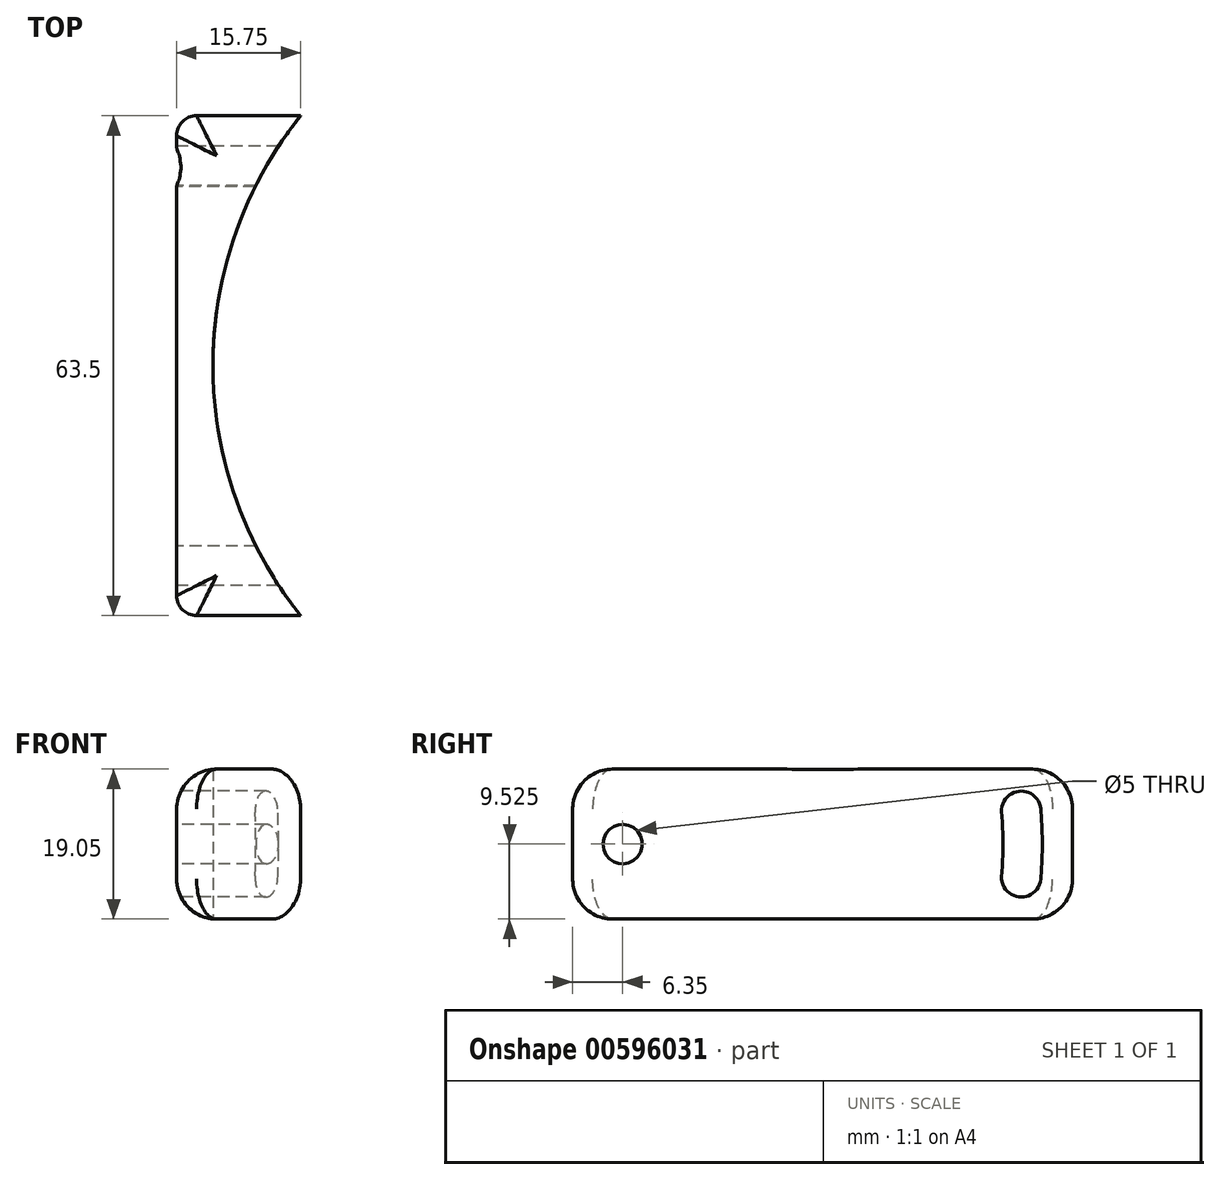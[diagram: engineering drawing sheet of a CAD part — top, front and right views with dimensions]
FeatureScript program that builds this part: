
annotation { "Feature Type Name" : "Feature", "Feature Type Description" : "" }
export const myFeature = defineFeature(function(context is Context, id is Id, definition is map)
    precondition{}
    {
        {
            var Q0;
            Q0=qCreatedBy(makeId("Top.planeOp"),FACE);
            var sketch = newSketch(context, id + "F0", { "sketchPlane" : qUnion([Q0])});
            skArc(sketch, "E0", {"start": v(-39.66, 31.75) * mm, "mid": v(-50.8, 0) * mm, "end": v(-39.66, -31.75) * mm});
            skLineSegment(sketch, "E1", {"start": v(-55.4, 29.21) * mm, "end": v(-55.4, -29.21) * mm});
            skPoint(sketch, "E2", {"position": v(-55.4, 0) * mm});
            skLineSegment(sketch, "E3", {"start": v(-52.87, 31.75) * mm, "end": v(-39.66, 31.75) * mm});
            skLineSegment(sketch, "E4", {"start": v(-52.87, -31.75) * mm, "end": v(-39.66, -31.75) * mm});
            skPoint(sketch, "E5.visualSharp", {"position": v(-55.4, 31.75) * mm});
            skArc(sketch, "E5.filletArc", {"start": v(-52.87, 31.75) * mm, "mid": v(-54.67, 31) * mm, "end": v(-55.4, 29.21) * mm});
            skPoint(sketch, "E6.visualSharp", {"position": v(-55.4, -31.75) * mm});
            skArc(sketch, "E6.filletArc", {"start": v(-55.4, -29.21) * mm, "mid": v(-54.67, -31) * mm, "end": v(-52.87, -31.75) * mm});
            skSolve(sketch);
        }
        {
            var Q0;
            Q0=makeQuery(id+"F0.imprint","IMPRINT",FACE,{"disambiguationData":[TD([[makeQuery(id+"F0.imprint","IMPRINT",EDGE,{"derivedFrom":sQuery(id+"F0.wireOp",EDGE,"E0")}),-1.0]])]});
            extrude(context, id + "F1", {"entities" : qUnion([Q0]), "depth" : 19.05 * mm, "offsetDistance" : 25.4 * mm});
        }
        {
            var Q0;
            Q0=makeQuery(id+"F1.opExtrude","SWEPT_FACE",FACE,{"disambiguationData":[OSD([sQuery(id+"F0.wireOp",EDGE,"E1")])]});
            cPlane(context, id + "F2", {"entities" : qUnion([Q0]), "cplaneType" : CPlaneType.OFFSET, "offset" : 0 * mm, "width" : 152.4 * mm, "height" : 152.4 * mm});
        }
        {
            var Q0;
            Q0=qCreatedBy(id+"F2.planeOp",FACE);
            var sketch = newSketch(context, id + "F3", { "sketchPlane" : qUnion([Q0])});
            skLineSegment(sketch, "E7", {"start": v(-31.75, 19.05) * mm, "end": v(-31.75, 0) * mm});
            skPoint(sketch, "E8", {"position": v(-31.75, 9.53) * mm});
            skLineSegment(sketch, "E9", {"start": v(-31.75, 9.53) * mm, "end": v(26.81, 9.53) * mm});
            skPoint(sketch, "E10", {"position": v(-25.4, 9.53) * mm});
            skPoint(sketch, "E11", {"position": v(25.4, 9.53) * mm});
            skArc(sketch, "E12", {"start": v(-22.73, 13.55) * mm, "mid": v(-25.02, 16.25) * mm, "end": v(-27.72, 13.97) * mm});
            skArc(sketch, "E13.MirrorCS", {"start": v(-22.73, 5.5) * mm, "mid": v(-25.02, 2.8) * mm, "end": v(-27.72, 5.08) * mm});
            skPoint(sketch, "E14.MirrorCS.end.orphan", {"position": v(-27.9, 9.53) * mm});
            skPoint(sketch, "E14.MirrorCS.start.orphan", {"position": v(-27.72, 5.08) * mm});
            skPoint(sketch, "E15.MirrorCS.end.orphan", {"position": v(-22.9, 9.53) * mm});
            skPoint(sketch, "E15.MirrorCS.start.orphan", {"position": v(-22.73, 5.5) * mm});
            skArc(sketch, "E16", {"start": v(-22.73, 13.55) * mm, "mid": v(-22.9, 9.53) * mm, "end": v(-22.73, 5.5) * mm});
            skArc(sketch, "E17", {"start": v(-27.72, 13.97) * mm, "mid": v(-27.9, 9.53) * mm, "end": v(-27.72, 5.08) * mm});
            skSolve(sketch);
        }
        {
            var Q0;
            Q0=sQuery(id+"F3.wireOp",VERTEX,"E11");
            var Q1;
            Q1=makeQuery(id+"F1.opExtrude","SWEPT_BODY",BODY,{"disambiguationData":[OSD([sQuery(id+"F0.wireOp",EDGE,"E0"),sQuery(id+"F0.wireOp",EDGE,"E1"),sQuery(id+"F0.wireOp",EDGE,"E3"),sQuery(id+"F0.wireOp",EDGE,"E4")])]});
            hole(context, id + "F4", {"style" : HoleStyle.SIMPLE, "endStyle" : HoleEndStyle.BLIND, "standardTappedOrClearance" : lookupTablePath({ "standard" : "ISO", "engagement" : "75%", "pitch" : "1 mm", "size" : "M6", "type" : "Tapped" }), "standardBlindInLast" : lookupTablePath({ "standard" : "ISO", "engagement" : "75%", "pitch" : "1 mm", "size" : "M6", "type" : "Tapped" }), "holeDiameter" : 5 * mm, "showTappedDepth" : true, "holeDepth" : 15.7 * mm, "isTappedThrough" : true, "tappedDepth" : 12.7 * mm, "tapClearance" : 3, "locations" : qUnion([Q0]), "scope" : qUnion([Q1]), "majorDiameter" : 6 * mm});
        }
        {
            var Q0;
            Q0=qSketchRegion(id+"F3",true);
            extrude(context, id + "F5", {"entities" : qUnion([Q0]), "operationType" : NewBodyOperationType.REMOVE, "oppositeDirection" : true, "depth" : 25.4 * mm, "offsetDistance" : 25.4 * mm});
        }
        {
            var Q0;
            Q0=makeQuery(id+"F1.opExtrude","CAP_EDGE",EDGE,{"disambiguationData":[OSD([sQuery(id+"F0.wireOp",EDGE,"E1")])],"isStart":false});
            var Q1;
            Q1=makeQuery(id+"F1.opExtrude","CAP_EDGE",EDGE,{"disambiguationData":[OSD([sQuery(id+"F0.wireOp",EDGE,"E1")])],"isStart":true});
            fillet(context, id + "F6", {"entities" : qUnion([Q0, Q1]), "radius" : 5.08 * mm, "tangentPropagation" : true, "allowEdgeOverflow" : false});
        }
    });
